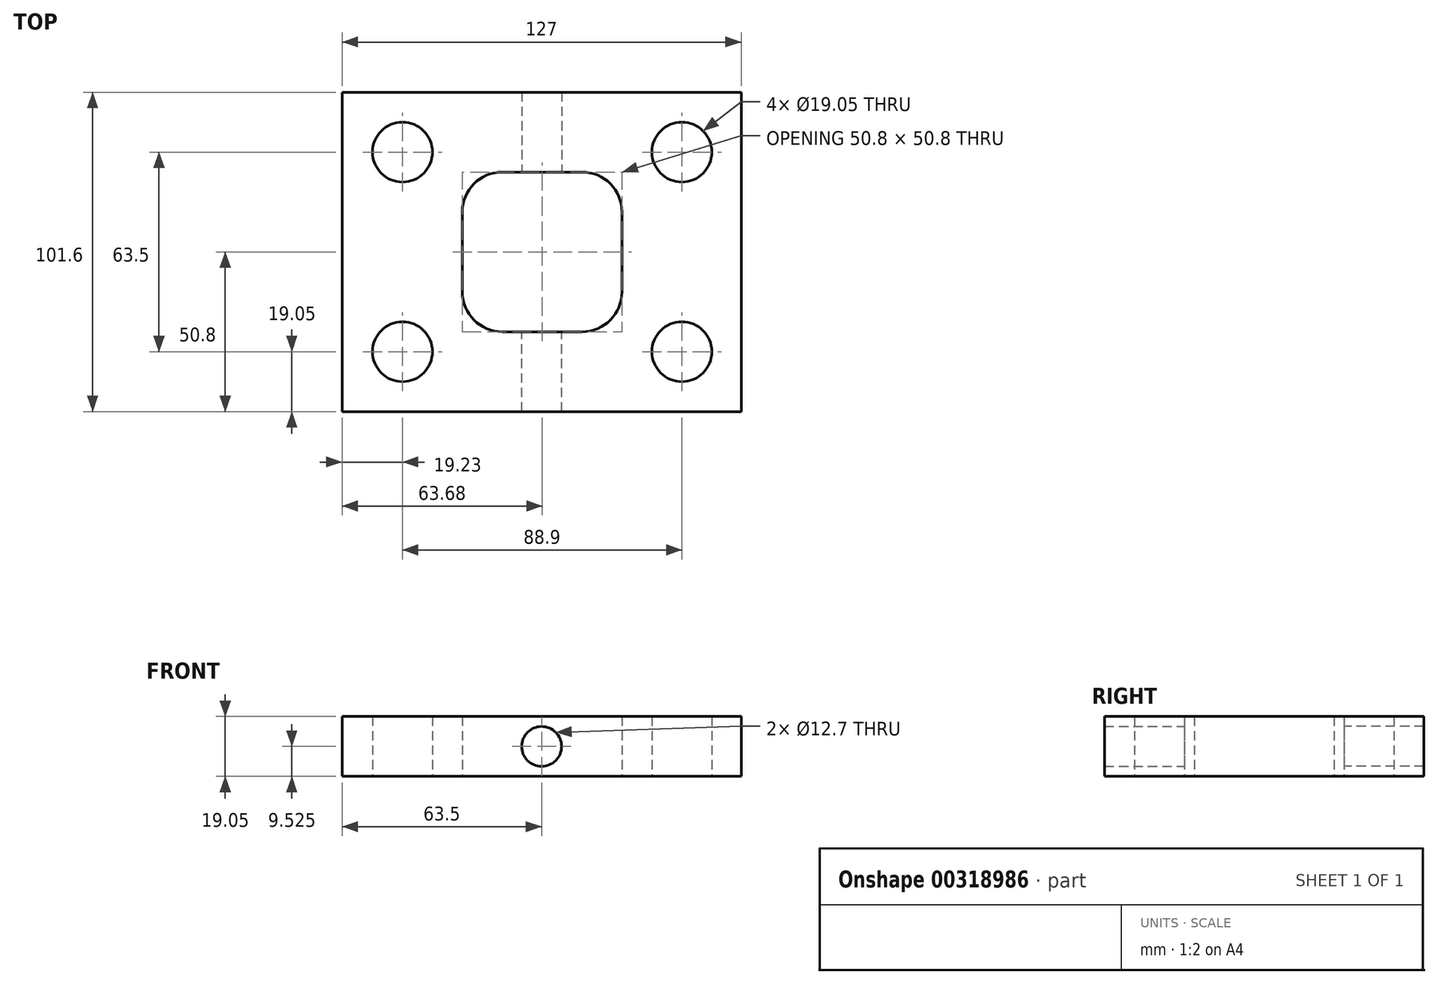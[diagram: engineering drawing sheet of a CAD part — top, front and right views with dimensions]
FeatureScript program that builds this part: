
annotation { "Feature Type Name" : "Feature", "Feature Type Description" : "" }
export const myFeature = defineFeature(function(context is Context, id is Id, definition is map)
    precondition{}
    {
        {
            var Q0;
            Q0=qCreatedBy(makeId("Top.planeOp"),FACE);
            var sketch = newSketch(context, id + "F0", { "sketchPlane" : qUnion([Q0])});
            skLineSegment(sketch, "E0", {"start": v(-63.5, 0) * mm, "end": v(-63.5, 50.8) * mm});
            skLineSegment(sketch, "E1", {"start": v(-63.5, 50.8) * mm, "end": v(0, 50.8) * mm});
            skLineSegment(sketch, "E2", {"start": v(63.5, 0) * mm, "end": v(63.5, 50.8) * mm});
            skLineSegment(sketch, "E3", {"start": v(63.5, 50.8) * mm, "end": v(0, 50.8) * mm});
            skLineSegment(sketch, "E4", {"start": v(-63.5, 0) * mm, "end": v(-63.5, -50.8) * mm});
            skLineSegment(sketch, "E5", {"start": v(-63.5, -50.8) * mm, "end": v(0, -50.8) * mm});
            skLineSegment(sketch, "E6", {"start": v(63.5, -50.8) * mm, "end": v(63.5, 0) * mm});
            skLineSegment(sketch, "E7", {"start": v(0, -50.8) * mm, "end": v(63.5, -50.8) * mm});
            skLineSegment(sketch, "E8.bottom", {"start": v(-12.52, 25.4) * mm, "end": v(12.88, 25.4) * mm});
            skLineSegment(sketch, "E8.top", {"start": v(-12.52, -25.4) * mm, "end": v(12.88, -25.4) * mm});
            skLineSegment(sketch, "E8.left", {"start": v(-25.22, 12.7) * mm, "end": v(-25.22, -12.7) * mm});
            skLineSegment(sketch, "E8.right", {"start": v(25.58, 12.7) * mm, "end": v(25.58, -12.7) * mm});
            skPoint(sketch, "E9.visualSharp", {"position": v(-25.22, 25.4) * mm});
            skArc(sketch, "E9.filletArc", {"start": v(-12.52, 25.4) * mm, "mid": v(-21.5, 21.68) * mm, "end": v(-25.22, 12.7) * mm});
            skPoint(sketch, "E10.visualSharp", {"position": v(25.58, 25.4) * mm});
            skArc(sketch, "E10.filletArc", {"start": v(25.58, 12.7) * mm, "mid": v(21.86, 21.68) * mm, "end": v(12.88, 25.4) * mm});
            skPoint(sketch, "E11.visualSharp", {"position": v(25.58, -25.4) * mm});
            skArc(sketch, "E11.filletArc", {"start": v(12.88, -25.4) * mm, "mid": v(21.86, -21.68) * mm, "end": v(25.58, -12.7) * mm});
            skPoint(sketch, "E12.visualSharp", {"position": v(-25.22, -25.4) * mm});
            skArc(sketch, "E12.filletArc", {"start": v(-25.22, -12.7) * mm, "mid": v(-21.5, -21.68) * mm, "end": v(-12.52, -25.4) * mm});
            skPoint(sketch, "E13.endSnap0", {"position": v(-25.22, 0) * mm});
            skCircle(sketch, "E14", {"center": v(-44.27, 31.75) * mm, "radius": 9.53 * mm});
            skPoint(sketch, "E15.endSnap0", {"position": v(25.58, 0) * mm});
            skCircle(sketch, "E16", {"center": v(44.63, 31.75) * mm, "radius": 9.53 * mm});
            skCircle(sketch, "E17.MirrorC", {"center": v(-44.27, -31.75) * mm, "radius": 9.53 * mm});
            skCircle(sketch, "E18.MirrorC", {"center": v(44.63, -31.75) * mm, "radius": 9.53 * mm});
            skSolve(sketch);
        }
        {
            var Q0;
            Q0=makeQuery(id+"F0.imprint","IMPRINT",FACE,{"disambiguationData":[TD([[makeQuery(id+"F0.imprint","IMPRINT",EDGE,{"derivedFrom":sQuery(id+"F0.wireOp",EDGE,"E0")}),-1.0]])]});
            extrude(context, id + "F1", {"entities" : qUnion([Q0]), "depth" : 19.05 * mm});
        }
        {
            var Q0;
            Q0=qCreatedBy(makeId("Front.planeOp"),FACE);
            var sketch = newSketch(context, id + "F2", { "sketchPlane" : qUnion([Q0])});
            skPoint(sketch, "E19", {"position": v(0, 9.53) * mm});
            skSolve(sketch);
        }
        {
            var Q0;
            Q0=sQuery(id+"F2.wireOp",VERTEX,"E19");
            var Q1;
            Q1=makeQuery(id+"F1.opExtrude","SWEPT_BODY",BODY,{"disambiguationData":[OSD([sQuery(id+"F0.wireOp",EDGE,"E0"),sQuery(id+"F0.wireOp",EDGE,"E1"),sQuery(id+"F0.wireOp",EDGE,"E2"),sQuery(id+"F0.wireOp",EDGE,"E3"),sQuery(id+"F0.wireOp",EDGE,"E4"),sQuery(id+"F0.wireOp",EDGE,"E5"),sQuery(id+"F0.wireOp",EDGE,"E6"),sQuery(id+"F0.wireOp",EDGE,"E7"),sQuery(id+"F0.wireOp",EDGE,"E8.bottom"),sQuery(id+"F0.wireOp",EDGE,"E8.top"),sQuery(id+"F0.wireOp",EDGE,"E8.left"),sQuery(id+"F0.wireOp",EDGE,"E8.right"),sQuery(id+"F0.wireOp",EDGE,"E9.filletArc"),sQuery(id+"F0.wireOp",EDGE,"E10.filletArc"),sQuery(id+"F0.wireOp",EDGE,"E11.filletArc"),sQuery(id+"F0.wireOp",EDGE,"E12.filletArc"),sQuery(id+"F0.wireOp",EDGE,"E14"),sQuery(id+"F0.wireOp",EDGE,"E16"),sQuery(id+"F0.wireOp",EDGE,"E17.MirrorC"),sQuery(id+"F0.wireOp",EDGE,"E18.MirrorC")])]});
            hole(context, id + "F3", {"style" : HoleStyle.SIMPLE, "endStyle" : HoleEndStyle.BLIND, "holeDiameter" : 12.7 * mm, "holeDepth" : 101.6 * mm, "tappedDepth" : 12.7 * mm, "tapClearance" : 3, "startFromSketch" : true, "locations" : qUnion([Q0]), "scope" : qUnion([Q1])});
        }
        {
            var Q0;
            Q0=qCreatedBy(makeId("Front.planeOp"),FACE);
            var sketch = newSketch(context, id + "F4", { "sketchPlane" : qUnion([Q0])});
            skPoint(sketch, "E20", {"position": v(0, 9.53) * mm});
            skSolve(sketch);
        }
        {
            var Q0;
            Q0=sQuery(id+"F4.wireOp",VERTEX,"E20");
            var Q1;
            Q1=makeQuery(id+"F1.opExtrude","SWEPT_BODY",BODY,{"disambiguationData":[OSD([sQuery(id+"F0.wireOp",EDGE,"E0"),sQuery(id+"F0.wireOp",EDGE,"E1"),sQuery(id+"F0.wireOp",EDGE,"E2"),sQuery(id+"F0.wireOp",EDGE,"E3"),sQuery(id+"F0.wireOp",EDGE,"E4"),sQuery(id+"F0.wireOp",EDGE,"E5"),sQuery(id+"F0.wireOp",EDGE,"E6"),sQuery(id+"F0.wireOp",EDGE,"E7"),sQuery(id+"F0.wireOp",EDGE,"E8.bottom"),sQuery(id+"F0.wireOp",EDGE,"E8.top"),sQuery(id+"F0.wireOp",EDGE,"E8.left"),sQuery(id+"F0.wireOp",EDGE,"E8.right"),sQuery(id+"F0.wireOp",EDGE,"E9.filletArc"),sQuery(id+"F0.wireOp",EDGE,"E10.filletArc"),sQuery(id+"F0.wireOp",EDGE,"E11.filletArc"),sQuery(id+"F0.wireOp",EDGE,"E12.filletArc"),sQuery(id+"F0.wireOp",EDGE,"E14"),sQuery(id+"F0.wireOp",EDGE,"E16"),sQuery(id+"F0.wireOp",EDGE,"E17.MirrorC"),sQuery(id+"F0.wireOp",EDGE,"E18.MirrorC")])]});
            hole(context, id + "F5", {"style" : HoleStyle.SIMPLE, "endStyle" : HoleEndStyle.BLIND, "oppositeDirection" : true, "holeDiameter" : 12.7 * mm, "holeDepth" : 254 * mm, "tappedDepth" : 12.7 * mm, "tapClearance" : 3, "startFromSketch" : true, "locations" : qUnion([Q0]), "scope" : qUnion([Q1])});
        }
    });
